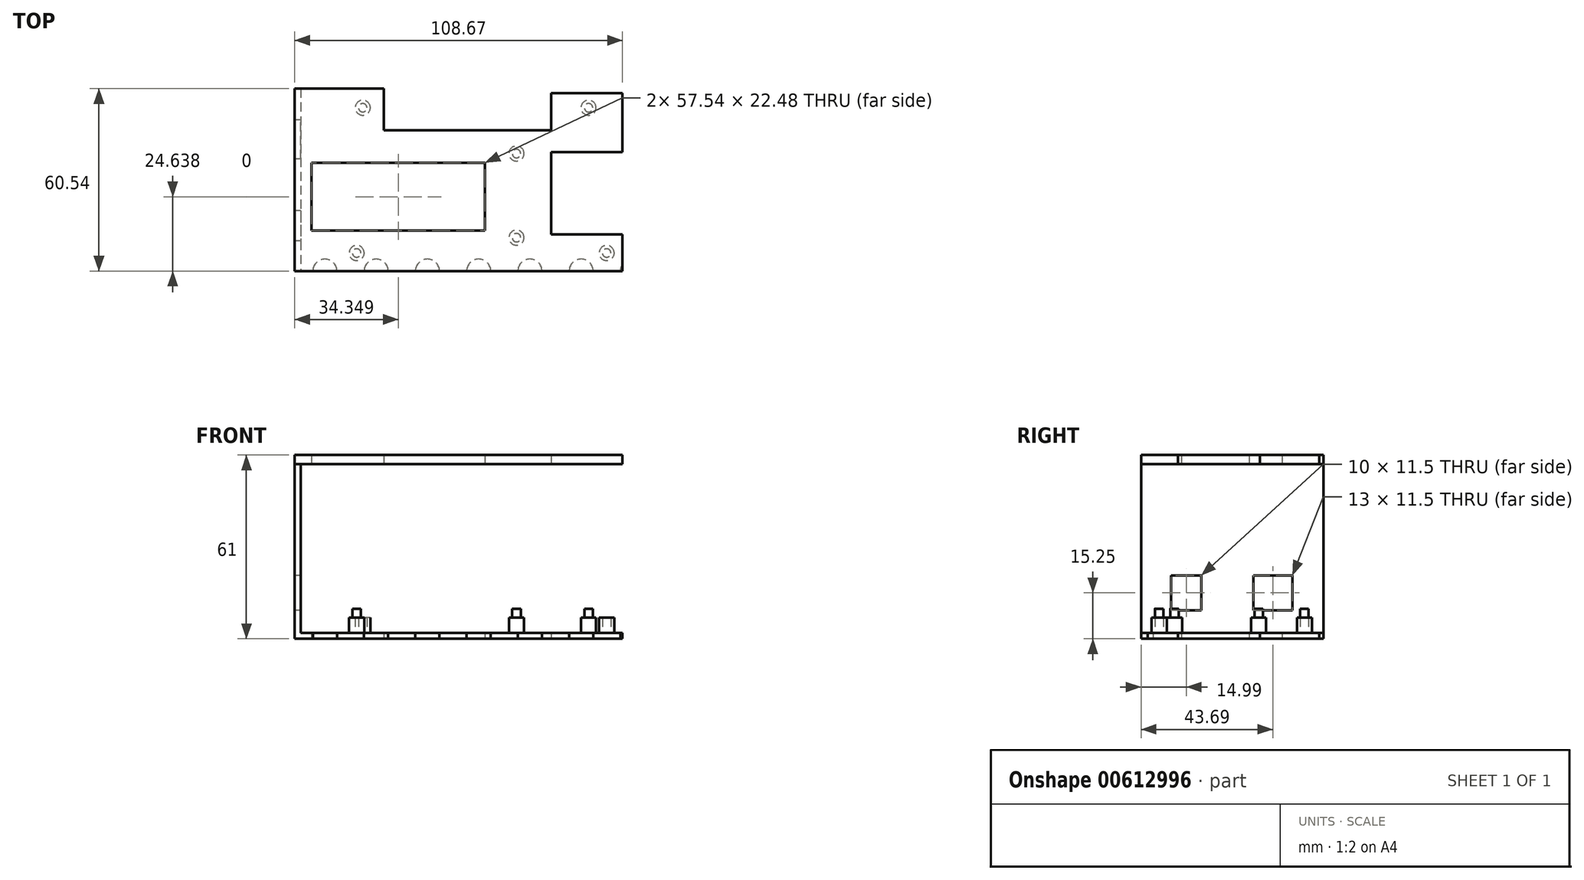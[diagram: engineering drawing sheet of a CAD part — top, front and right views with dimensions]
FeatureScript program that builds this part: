
annotation { "Feature Type Name" : "Feature", "Feature Type Description" : "" }
export const myFeature = defineFeature(function(context is Context, id is Id, definition is map)
    precondition{}
    {
        {
            var Q0;
            Q0=qCreatedBy(makeId("Top.planeOp"),FACE);
            var sketch = newSketch(context, id + "F0", { "sketchPlane" : qUnion([Q0])});
            skLineSegment(sketch, "E0.bottom", {"start": v(-60, 45) * mm, "end": v(60, 45) * mm});
            skLineSegment(sketch, "E0.top", {"start": v(-60, -45) * mm, "end": v(60, -45) * mm});
            skLineSegment(sketch, "E0.left", {"start": v(-60, 45) * mm, "end": v(-60, -45) * mm});
            skLineSegment(sketch, "E0.right", {"start": v(60, 45) * mm, "end": v(60, -45) * mm});
            skPoint(sketch, "E0.middle", {"position": v(0, 0) * mm});
            skLineSegment(sketch, "E1.0", {"start": v(-62, 47) * mm, "end": v(-62, -47) * mm});
            skLineSegment(sketch, "E1.1", {"start": v(-62, 47) * mm, "end": v(62, 47) * mm});
            skLineSegment(sketch, "E1.2", {"start": v(62, 47) * mm, "end": v(62, -47) * mm});
            skLineSegment(sketch, "E1.3", {"start": v(-62, -47) * mm, "end": v(62, -47) * mm});
            skLineSegment(sketch, "E2", {"start": v(60, 31) * mm, "end": v(60, 29) * mm});
            skSolve(sketch);
        }
        {
            var Q0;
            Q0 = qSketchRegion(id + "F0", true);
            var Q1;
            Q1=makeQuery(id+"F0.imprint","IMPRINT",FACE,{"disambiguationData":[TD([[makeQuery(id+"F0.imprint","IMPRINT",EDGE,{"derivedFrom":sQuery(id+"F0.wireOp",EDGE,"E0.bottom")}),-1.0]])]});
            var Q2;
            {var subQ0=sQuery(id+"F0.wireOp",EDGE,"MuUvbIVO-RKHI-1Iq4-MDRf-3431R1IhVsWr");Q2=makeQuery(id+"F0.imprint","IMPRINT",FACE,{"disambiguationData":[TD([[makeQuery(id+"F0.imprint","IMPRINT",EDGE,{"derivedFrom":subQ0}),1.0]])]});}
            var Q3;
            {var subQ0=sQuery(id+"F0.wireOp",EDGE,"E0.top");Q3=makeQuery(id+"F0.imprint","IMPRINT",FACE,{"disambiguationData":[TD([[makeQuery(id+"F0.imprint","IMPRINT",EDGE,{"derivedFrom":subQ0}),1.0]])]});}
            extrude(context, id + "F1", {"entities" : qUnion([Q0, Q1, Q2, Q3]), "depth" : 2 * mm, "offsetDistance" : 25 * mm});
        }
        {
            var Q0;
            Q0=makeQuery(id+"F0.imprint","IMPRINT",FACE,{"disambiguationData":[TD([[makeQuery(id+"F0.imprint","IMPRINT",EDGE,{"derivedFrom":sQuery(id+"F0.wireOp",EDGE,"E0.bottom")}),1.0]])]});
            var Q1;
            {var subQ0=sQuery(id+"F0.wireOp",EDGE,"MuUvbIVO-RKHI-1Iq4-MDRf-3431R1IhVsWr");Q1=makeQuery(id+"F0.imprint","IMPRINT",FACE,{"disambiguationData":[TD([[makeQuery(id+"F0.imprint","IMPRINT",EDGE,{"derivedFrom":subQ0}),1.0]])]});}
            extrude(context, id + "F2", {"entities" : qUnion([Q0, Q1]), "operationType" : NewBodyOperationType.ADD, "depth" : 58 * mm, "offsetDistance" : 25 * mm});
        }
        {
            var Q0;
            Q0=makeQuery(id+"F1.opExtrude","CAP_FACE",FACE,{"disambiguationData":[OSD([sQuery(id+"F0.wireOp",EDGE,"E1.0"),sQuery(id+"F0.wireOp",EDGE,"E1.1"),sQuery(id+"F0.wireOp",EDGE,"E1.2"),sQuery(id+"F0.wireOp",EDGE,"E1.3")])],"isStart":false});
            var sketch = newSketch(context, id + "F3", { "sketchPlane" : qUnion([Q0])});
            skCircle(sketch, "E3", {"center": v(35.45, 23.2) * mm, "radius": 2.5 * mm});
            skCircle(sketch, "E4", {"center": v(11.55, -19.9) * mm, "radius": 2.5 * mm});
            skCircle(sketch, "E5", {"center": v(41.45, -25) * mm, "radius": 2.5 * mm});
            skCircle(sketch, "E6", {"center": v(11.55, 8) * mm, "radius": 2.5 * mm});
            skCircle(sketch, "E7", {"center": v(-39.45, 23.2) * mm, "radius": 2.5 * mm});
            skCircle(sketch, "E8", {"center": v(-41.45, -25) * mm, "radius": 2.5 * mm});
            skSolve(sketch);
        }
        {
            var Q0;
            Q0 = qSketchRegion(id + "F3", true);
            extrude(context, id + "F4", {"entities" : qUnion([Q0]), "operationType" : NewBodyOperationType.ADD, "depth" : 5 * mm, "offsetDistance" : 25 * mm});
        }
        {
            var Q0;
            Q0=makeQuery(id+"F4.opExtrude","CAP_FACE",FACE,{"disambiguationData":[OSD([sQuery(id+"F3.wireOp",EDGE,"E7")])],"isStart":false});
            var sketch = newSketch(context, id + "F5", { "sketchPlane" : qUnion([Q0])});
            skPoint(sketch, "E9", {"position": v(-39.45, 23.2) * mm});
            skPoint(sketch, "E10", {"position": v(-41.45, -25) * mm});
            skPoint(sketch, "E11", {"position": v(11.55, 8) * mm});
            skPoint(sketch, "E12", {"position": v(11.55, -19.9) * mm});
            skPoint(sketch, "E13", {"position": v(41.45, -25) * mm});
            skPoint(sketch, "E14", {"position": v(35.45, 23.2) * mm});
            skCircle(sketch, "E15", {"center": v(-39.45, 23.2) * mm, "radius": 1.4 * mm});
            skCircle(sketch, "E16", {"center": v(-41.45, -25) * mm, "radius": 1.4 * mm});
            skCircle(sketch, "E17", {"center": v(11.55, 8) * mm, "radius": 1.4 * mm});
            skCircle(sketch, "E18", {"center": v(11.55, -19.9) * mm, "radius": 1.4 * mm});
            skCircle(sketch, "E19", {"center": v(41.45, -25) * mm, "radius": 1.4 * mm});
            skCircle(sketch, "E20", {"center": v(35.45, 23.2) * mm, "radius": 1.4 * mm});
            skSolve(sketch);
        }
        {
            var Q0;
            Q0=makeQuery(id+"F5.imprint","IMPRINT",FACE,{"disambiguationData":[TD([[makeQuery(id+"F5.imprint","IMPRINT",EDGE,{"derivedFrom":sQuery(id+"F5.wireOp",EDGE,"E20")}),1.0]])]});
            var Q1;
            Q1=makeQuery(id+"F5.imprint","IMPRINT",FACE,{"disambiguationData":[TD([[makeQuery(id+"F5.imprint","IMPRINT",EDGE,{"derivedFrom":sQuery(id+"F5.wireOp",EDGE,"E17")}),1.0]])]});
            var Q2;
            Q2=makeQuery(id+"F5.imprint","IMPRINT",FACE,{"disambiguationData":[TD([[makeQuery(id+"F5.imprint","IMPRINT",EDGE,{"derivedFrom":sQuery(id+"F5.wireOp",EDGE,"E18")}),1.0]])]});
            var Q3;
            Q3=makeQuery(id+"F5.imprint","IMPRINT",FACE,{"disambiguationData":[TD([[makeQuery(id+"F5.imprint","IMPRINT",EDGE,{"derivedFrom":sQuery(id+"F5.wireOp",EDGE,"E16")}),1.0]])]});
            extrude(context, id + "F6", {"entities" : qUnion([Q0, Q1, Q2, Q3]), "operationType" : NewBodyOperationType.ADD, "depth" : 3 * mm, "offsetDistance" : 25 * mm});
        }
        {
            var Q0;
            Q0=sQuery(id+"F3.wireOp",VERTEX,"E7.center");
            var Q1;
            Q1=sQuery(id+"F3.wireOp",VERTEX,"E5.center");
            var Q2;
            Q2=makeQuery(id+"F1.opExtrude","SWEPT_BODY",BODY,{"disambiguationData":[OSD([sQuery(id+"F0.wireOp",EDGE,"E1.0"),sQuery(id+"F0.wireOp",EDGE,"E1.1"),sQuery(id+"F0.wireOp",EDGE,"E1.2"),sQuery(id+"F0.wireOp",EDGE,"E1.3")])]});
            hole(context, id + "F7", {"style" : HoleStyle.SIMPLE, "endStyle" : HoleEndStyle.BLIND, "oppositeDirection" : true, "holeDiameter" : 2.8 * mm, "majorDiameter" : 5 * mm, "holeDepth" : 5 * mm, "isTappedThrough" : true, "tappedDepth" : 12 * mm, "tapClearance" : 3, "startFromSketch" : true, "locations" : qUnion([Q0, Q1]), "scope" : qUnion([Q2])});
        }
        {
            var Q0;
            Q0=makeQuery(id+"F1.opExtrude","CAP_FACE",FACE,{"disambiguationData":[OSD([sQuery(id+"F0.wireOp",EDGE,"E1.0"),sQuery(id+"F0.wireOp",EDGE,"E1.1"),sQuery(id+"F0.wireOp",EDGE,"E1.2"),sQuery(id+"F0.wireOp",EDGE,"E1.3")])],"isStart":true});
            var sketch = newSketch(context, id + "F8", { "sketchPlane" : qUnion([Q0])});
            skLineSegment(sketch, "E21", {"start": v(-52, 107.06) * mm, "end": v(-52, 15.89) * mm, "construction": true});
            skLineSegment(sketch, "E22", {"start": v(-52, 47) * mm, "end": v(-56, 47) * mm});
            skLineSegment(sketch, "E23", {"start": v(-56, 47) * mm, "end": v(-56, 31) * mm});
            skArc(sketch, "E24", {"start": v(-56, 31) * mm, "mid": v(-54.83, 28.17) * mm, "end": v(-52, 27) * mm});
            skLineSegment(sketch, "E25", {"start": v(-52, 47) * mm, "end": v(-52, 27) * mm});
            skLineSegment(sketch, "E26.MirrorCS", {"start": v(-48, 47) * mm, "end": v(-48, 31) * mm});
            skLineSegment(sketch, "E27.MirrorCS", {"start": v(-52, 47) * mm, "end": v(-48, 47) * mm});
            skArc(sketch, "E28.MirrorCS", {"start": v(-48, 31) * mm, "mid": v(-49.17, 28.17) * mm, "end": v(-52, 27) * mm});
            skLineSegment(sketch, "E29.1.0.0", {"start": v(-35, 47) * mm, "end": v(-39, 47) * mm});
            skLineSegment(sketch, "E29.1.0.1", {"start": v(-39, 47) * mm, "end": v(-39, 31) * mm});
            skLineSegment(sketch, "E29.1.0.2", {"start": v(-31, 47) * mm, "end": v(-31, 31) * mm});
            skArc(sketch, "E29.1.0.3", {"start": v(-31, 31) * mm, "mid": v(-32.17, 28.17) * mm, "end": v(-35, 27) * mm});
            skArc(sketch, "E29.1.0.4", {"start": v(-39, 31) * mm, "mid": v(-37.83, 28.17) * mm, "end": v(-35, 27) * mm});
            skLineSegment(sketch, "E29.2.0.0", {"start": v(-18, 47) * mm, "end": v(-22, 47) * mm});
            skLineSegment(sketch, "E29.2.0.1", {"start": v(-22, 47) * mm, "end": v(-22, 31) * mm});
            skLineSegment(sketch, "E29.2.0.2", {"start": v(-14, 47) * mm, "end": v(-14, 31) * mm});
            skArc(sketch, "E29.2.0.3", {"start": v(-14, 31) * mm, "mid": v(-15.17, 28.17) * mm, "end": v(-18, 27) * mm});
            skArc(sketch, "E29.2.0.4", {"start": v(-22, 31) * mm, "mid": v(-20.83, 28.17) * mm, "end": v(-18, 27) * mm});
            skLineSegment(sketch, "E29.3.0.0", {"start": v(-1, 47) * mm, "end": v(-5, 47) * mm});
            skLineSegment(sketch, "E29.3.0.1", {"start": v(-5, 47) * mm, "end": v(-5, 31) * mm});
            skLineSegment(sketch, "E29.3.0.2", {"start": v(3, 47) * mm, "end": v(3, 31) * mm});
            skArc(sketch, "E29.3.0.3", {"start": v(3, 31) * mm, "mid": v(1.83, 28.17) * mm, "end": v(-1, 27) * mm});
            skArc(sketch, "E29.3.0.4", {"start": v(-5, 31) * mm, "mid": v(-3.83, 28.17) * mm, "end": v(-1, 27) * mm});
            skLineSegment(sketch, "E29.4.0.0", {"start": v(16, 47) * mm, "end": v(12, 47) * mm});
            skLineSegment(sketch, "E29.4.0.1", {"start": v(12, 47) * mm, "end": v(12, 31) * mm});
            skLineSegment(sketch, "E29.4.0.2", {"start": v(20, 47) * mm, "end": v(20, 31) * mm});
            skArc(sketch, "E29.4.0.3", {"start": v(20, 31) * mm, "mid": v(18.83, 28.17) * mm, "end": v(16, 27) * mm});
            skArc(sketch, "E29.4.0.4", {"start": v(12, 31) * mm, "mid": v(13.17, 28.17) * mm, "end": v(16, 27) * mm});
            skLineSegment(sketch, "E29.direction1", {"start": v(-56, 47) * mm, "end": v(-39, 47) * mm, "construction": true});
            skLineSegment(sketch, "E30.0.5.0", {"start": v(33, 47) * mm, "end": v(29, 47) * mm});
            skLineSegment(sketch, "E30.3.5.0", {"start": v(29, 47) * mm, "end": v(29, 31) * mm});
            skLineSegment(sketch, "E30.6.5.0", {"start": v(37, 47) * mm, "end": v(37, 31) * mm});
            skArc(sketch, "E30.9.5.0", {"start": v(37, 31) * mm, "mid": v(35.83, 28.17) * mm, "end": v(33, 27) * mm});
            skArc(sketch, "E30.13.5.0", {"start": v(29, 31) * mm, "mid": v(30.17, 28.17) * mm, "end": v(33, 27) * mm});
            skLineSegment(sketch, "E30.0.6.0", {"start": v(50, 47) * mm, "end": v(46, 47) * mm});
            skLineSegment(sketch, "E30.3.6.0", {"start": v(46, 47) * mm, "end": v(46, 31) * mm});
            skLineSegment(sketch, "E30.6.6.0", {"start": v(54, 47) * mm, "end": v(54, 31) * mm});
            skArc(sketch, "E30.9.6.0", {"start": v(54, 31) * mm, "mid": v(52.83, 28.17) * mm, "end": v(50, 27) * mm});
            skArc(sketch, "E30.13.6.0", {"start": v(46, 31) * mm, "mid": v(47.17, 28.17) * mm, "end": v(50, 27) * mm});
            skSolve(sketch);
        }
        {
            var Q0;
            Q0=makeQuery(id+"F8.imprint","IMPRINT",FACE,{"disambiguationData":[TD([[makeQuery(id+"F8.imprint","IMPRINT",EDGE,{"derivedFrom":sQuery(id+"F8.wireOp",EDGE,"E22")}),-1.0]])]});
            var Q1;
            Q1=makeQuery(id+"F8.imprint","IMPRINT",FACE,{"disambiguationData":[TD([[makeQuery(id+"F8.imprint","IMPRINT",EDGE,{"derivedFrom":sQuery(id+"F8.wireOp",EDGE,"E25")}),1.0]])]});
            var Q2;
            {var subQ0=sQuery(id+"F8.wireOp",EDGE,"E29.1.0.0");Q2=makeQuery(id+"F8.imprint","IMPRINT",FACE,{"disambiguationData":[TD([[makeQuery(id+"F8.imprint","IMPRINT",EDGE,{"derivedFrom":subQ0}),-1.0]])]});}
            var Q3;
            {var subQ1=sQuery(id+"F8.wireOp",EDGE,"E29.2.0.0");Q3=makeQuery(id+"F8.imprint","IMPRINT",FACE,{"disambiguationData":[TD([[makeQuery(id+"F8.imprint","IMPRINT",EDGE,{"derivedFrom":subQ1}),-1.0]])]});}
            var Q4;
            {var subQ1=sQuery(id+"F8.wireOp",EDGE,"E29.3.0.0");Q4=makeQuery(id+"F8.imprint","IMPRINT",FACE,{"disambiguationData":[TD([[makeQuery(id+"F8.imprint","IMPRINT",EDGE,{"derivedFrom":subQ1}),-1.0]])]});}
            var Q5;
            {var subQ1=sQuery(id+"F8.wireOp",EDGE,"E29.4.0.0");Q5=makeQuery(id+"F8.imprint","IMPRINT",FACE,{"disambiguationData":[TD([[makeQuery(id+"F8.imprint","IMPRINT",EDGE,{"derivedFrom":subQ1}),-1.0]])]});}
            var Q6;
            {var subQ1=sQuery(id+"F8.wireOp",EDGE,"E30.0.5.0");Q6=makeQuery(id+"F8.imprint","IMPRINT",FACE,{"disambiguationData":[TD([[makeQuery(id+"F8.imprint","IMPRINT",EDGE,{"derivedFrom":subQ1}),-1.0]])]});}
            var Q7;
            {var subQ1=sQuery(id+"F8.wireOp",EDGE,"E30.0.6.0");Q7=makeQuery(id+"F8.imprint","IMPRINT",FACE,{"disambiguationData":[TD([[makeQuery(id+"F8.imprint","IMPRINT",EDGE,{"derivedFrom":subQ1}),-1.0]])]});}
            extrude(context, id + "F9", {"entities" : qUnion([Q0, Q1, Q2, Q3, Q4, Q5, Q6, Q7]), "operationType" : NewBodyOperationType.REMOVE, "oppositeDirection" : true, "depth" : 8 * mm, "offsetDistance" : 25 * mm});
        }
        {
            var Q0;
            Q0=makeQuery(id+"F2.opExtrude","SWEPT_FACE",FACE,{"disambiguationData":[OSD([sQuery(id+"F0.wireOp",EDGE,"E0.bottom")])]});
            var sketch = newSketch(context, id + "F10", { "sketchPlane" : qUnion([Q0])});
            skLineSegment(sketch, "E31", {"start": v(-42.5, 52) * mm, "end": v(-42.5, 2) * mm});
            skLineSegment(sketch, "E32", {"start": v(-42.5, 2) * mm, "end": v(-41.5, 2) * mm});
            skLineSegment(sketch, "E33", {"start": v(-41.5, 2) * mm, "end": v(-41.5, 52) * mm});
            skLineSegment(sketch, "E34", {"start": v(-41.5, 52) * mm, "end": v(-42.5, 52) * mm});
            skLineSegment(sketch, "E35", {"start": v(-40, 64) * mm, "end": v(-40, -2.7) * mm, "construction": true});
            skLineSegment(sketch, "E36.MirrorCS", {"start": v(-38.5, 2) * mm, "end": v(-38.5, 52) * mm});
            skLineSegment(sketch, "E37.MirrorCS", {"start": v(-37.5, 52) * mm, "end": v(-37.5, 2) * mm});
            skLineSegment(sketch, "E38.MirrorCS", {"start": v(-38.5, 52) * mm, "end": v(-37.5, 52) * mm});
            skLineSegment(sketch, "E39.MirrorCS", {"start": v(-37.5, 2) * mm, "end": v(-38.5, 2) * mm});
            skLineSegment(sketch, "E40", {"start": v(-20, 58) * mm, "end": v(-20, 0) * mm, "construction": true});
            skLineSegment(sketch, "E41.MirrorCS", {"start": v(1.5, 52) * mm, "end": v(2.5, 52) * mm});
            skLineSegment(sketch, "E42.MirrorCS", {"start": v(2.5, 2) * mm, "end": v(1.5, 2) * mm});
            skLineSegment(sketch, "E43.MirrorCS", {"start": v(-2.5, 2) * mm, "end": v(-1.5, 2) * mm});
            skLineSegment(sketch, "E44.MirrorCS", {"start": v(-1.5, 52) * mm, "end": v(-2.5, 52) * mm});
            skLineSegment(sketch, "E45.MirrorCS", {"start": v(-1.5, 2) * mm, "end": v(-1.5, 52) * mm});
            skLineSegment(sketch, "E46.MirrorCS", {"start": v(1.5, 2) * mm, "end": v(1.5, 52) * mm});
            skLineSegment(sketch, "E47.MirrorCS", {"start": v(0, 64) * mm, "end": v(0, -2.7) * mm, "construction": true});
            skLineSegment(sketch, "E48.MirrorCS", {"start": v(2.5, 52) * mm, "end": v(2.5, 2) * mm});
            skLineSegment(sketch, "E49.MirrorCS", {"start": v(-2.5, 52) * mm, "end": v(-2.5, 2) * mm});
            skLineSegment(sketch, "E50", {"start": v(20, 58) * mm, "end": v(20, -6.5) * mm, "construction": true});
            skLineSegment(sketch, "E51.MirrorCS", {"start": v(38.5, 52) * mm, "end": v(37.5, 52) * mm});
            skLineSegment(sketch, "E52.MirrorCS", {"start": v(37.5, 2) * mm, "end": v(38.5, 2) * mm});
            skLineSegment(sketch, "E53.MirrorCS", {"start": v(41.5, 52) * mm, "end": v(42.5, 52) * mm});
            skLineSegment(sketch, "E54.MirrorCS", {"start": v(42.5, 2) * mm, "end": v(41.5, 2) * mm});
            skLineSegment(sketch, "E55.MirrorCS", {"start": v(42.5, 52) * mm, "end": v(42.5, 2) * mm});
            skLineSegment(sketch, "E56.MirrorCS", {"start": v(38.5, 2) * mm, "end": v(38.5, 52) * mm});
            skLineSegment(sketch, "E57.MirrorCS", {"start": v(37.5, 52) * mm, "end": v(37.5, 2) * mm});
            skLineSegment(sketch, "E58.MirrorCS", {"start": v(41.5, 2) * mm, "end": v(41.5, 52) * mm});
            skLineSegment(sketch, "E59.MirrorCS", {"start": v(40, 64) * mm, "end": v(40, -2.7) * mm, "construction": true});
            skSolve(sketch);
        }
        {
            var Q0;
            Q0 = qSketchRegion(id + "F10", true);
            extrude(context, id + "F11", {"entities" : qUnion([Q0]), "operationType" : NewBodyOperationType.ADD, "depth" : 3 * mm, "offsetDistance" : 25 * mm});
        }
        {
            var Q0;
            Q0=makeQuery(id+"F11.opExtrude","CAP_FACE",FACE,{"disambiguationData":[OSD([sQuery(id+"F10.wireOp",EDGE,"E31"),sQuery(id+"F10.wireOp",EDGE,"E32"),sQuery(id+"F10.wireOp",EDGE,"E33"),sQuery(id+"F10.wireOp",EDGE,"E34")])],"isStart":false});
            var sketch = newSketch(context, id + "F12", { "sketchPlane" : qUnion([Q0])});
            skLineSegment(sketch, "E60", {"start": v(-20, 58) * mm, "end": v(-20, 2) * mm});
            skLineSegment(sketch, "E61.MirrorCS", {"start": v(-2.5, 52) * mm, "end": v(2.5, 52) * mm});
            skLineSegment(sketch, "E62.MirrorCS", {"start": v(2.5, 49) * mm, "end": v(-2.5, 49) * mm});
            skLineSegment(sketch, "E63.MirrorCS", {"start": v(2.5, 49) * mm, "end": v(2.5, 52) * mm});
            skLineSegment(sketch, "E64.MirrorCS", {"start": v(-2.5, 49) * mm, "end": v(-2.5, 52) * mm});
            skLineSegment(sketch, "E65", {"start": v(20, 58) * mm, "end": v(20, 2) * mm});
            skLineSegment(sketch, "E66.0.1.0", {"start": v(-2.5, 41) * mm, "end": v(-2.5, 44) * mm});
            skLineSegment(sketch, "E66.0.1.1", {"start": v(2.5, 41) * mm, "end": v(2.5, 44) * mm});
            skLineSegment(sketch, "E66.0.1.2", {"start": v(2.5, 41) * mm, "end": v(-2.5, 41) * mm});
            skLineSegment(sketch, "E66.0.1.3", {"start": v(-2.5, 44) * mm, "end": v(2.5, 44) * mm});
            skLineSegment(sketch, "E66.0.2.0", {"start": v(-2.5, 34) * mm, "end": v(-2.5, 37) * mm});
            skLineSegment(sketch, "E66.0.2.1", {"start": v(2.5, 34) * mm, "end": v(2.5, 37) * mm});
            skLineSegment(sketch, "E66.0.2.2", {"start": v(2.5, 34) * mm, "end": v(-2.5, 34) * mm});
            skLineSegment(sketch, "E66.0.2.3", {"start": v(-2.5, 37) * mm, "end": v(2.5, 37) * mm});
            skLineSegment(sketch, "E66.0.3.0", {"start": v(-2.5, 26) * mm, "end": v(-2.5, 29) * mm});
            skLineSegment(sketch, "E66.0.3.1", {"start": v(2.5, 26) * mm, "end": v(2.5, 29) * mm});
            skLineSegment(sketch, "E66.0.3.2", {"start": v(2.5, 26) * mm, "end": v(-2.5, 26) * mm});
            skLineSegment(sketch, "E66.0.3.3", {"start": v(-2.5, 29) * mm, "end": v(2.5, 29) * mm});
            skLineSegment(sketch, "E66.0.4.0", {"start": v(-2.5, 18) * mm, "end": v(-2.5, 21) * mm});
            skLineSegment(sketch, "E66.0.4.1", {"start": v(2.5, 18) * mm, "end": v(2.5, 21) * mm});
            skLineSegment(sketch, "E66.0.4.2", {"start": v(2.5, 18) * mm, "end": v(-2.5, 18) * mm});
            skLineSegment(sketch, "E66.0.4.3", {"start": v(-2.5, 21) * mm, "end": v(2.5, 21) * mm});
            skLineSegment(sketch, "E66.0.5.0", {"start": v(-2.5, 10) * mm, "end": v(-2.5, 13) * mm});
            skLineSegment(sketch, "E66.0.5.1", {"start": v(2.5, 10) * mm, "end": v(2.5, 13) * mm});
            skLineSegment(sketch, "E66.0.5.2", {"start": v(2.5, 10) * mm, "end": v(-2.5, 10) * mm});
            skLineSegment(sketch, "E66.0.5.3", {"start": v(-2.5, 13) * mm, "end": v(2.5, 13) * mm});
            skLineSegment(sketch, "E66.direction2", {"start": v(-2.5, 49) * mm, "end": v(-2.5, 41) * mm, "construction": true});
            skLineSegment(sketch, "E67.MirrorCS", {"start": v(37.5, 18) * mm, "end": v(37.5, 21) * mm});
            skLineSegment(sketch, "E68.MirrorCS", {"start": v(37.5, 41) * mm, "end": v(37.5, 44) * mm});
            skLineSegment(sketch, "E69.MirrorCS", {"start": v(37.5, 49) * mm, "end": v(37.5, 52) * mm});
            skLineSegment(sketch, "E70.MirrorCS", {"start": v(37.5, 34) * mm, "end": v(37.5, 37) * mm});
            skLineSegment(sketch, "E71.MirrorCS", {"start": v(37.5, 26) * mm, "end": v(37.5, 29) * mm});
            skLineSegment(sketch, "E72.MirrorCS", {"start": v(42.5, 34) * mm, "end": v(42.5, 37) * mm});
            skLineSegment(sketch, "E73.MirrorCS", {"start": v(42.5, 41) * mm, "end": v(42.5, 44) * mm});
            skLineSegment(sketch, "E74.MirrorCS", {"start": v(42.5, 26) * mm, "end": v(42.5, 29) * mm});
            skLineSegment(sketch, "E75.MirrorCS", {"start": v(42.5, 10) * mm, "end": v(42.5, 13) * mm});
            skLineSegment(sketch, "E76.MirrorCS", {"start": v(42.5, 18) * mm, "end": v(42.5, 21) * mm});
            skLineSegment(sketch, "E77.MirrorCS", {"start": v(42.5, 49) * mm, "end": v(42.5, 52) * mm});
            skLineSegment(sketch, "E78.MirrorCS", {"start": v(37.5, 10) * mm, "end": v(37.5, 13) * mm});
            skLineSegment(sketch, "E79.MirrorCS", {"start": v(42.5, 21) * mm, "end": v(37.5, 21) * mm});
            skLineSegment(sketch, "E80.MirrorCS", {"start": v(42.5, 13) * mm, "end": v(37.5, 13) * mm});
            skLineSegment(sketch, "E81.MirrorCS", {"start": v(37.5, 10) * mm, "end": v(42.5, 10) * mm});
            skLineSegment(sketch, "E82.MirrorCS", {"start": v(42.5, 52) * mm, "end": v(37.5, 52) * mm});
            skLineSegment(sketch, "E83.MirrorCS", {"start": v(37.5, 18) * mm, "end": v(42.5, 18) * mm});
            skLineSegment(sketch, "E84.MirrorCS", {"start": v(37.5, 49) * mm, "end": v(42.5, 49) * mm});
            skLineSegment(sketch, "E85.MirrorCS", {"start": v(37.5, 26) * mm, "end": v(42.5, 26) * mm});
            skLineSegment(sketch, "E86.MirrorCS", {"start": v(37.5, 34) * mm, "end": v(42.5, 34) * mm});
            skLineSegment(sketch, "E87.MirrorCS", {"start": v(42.5, 29) * mm, "end": v(37.5, 29) * mm});
            skLineSegment(sketch, "E88.MirrorCS", {"start": v(37.5, 41) * mm, "end": v(42.5, 41) * mm});
            skLineSegment(sketch, "E89.MirrorCS", {"start": v(42.5, 49) * mm, "end": v(42.5, 41) * mm, "construction": true});
            skLineSegment(sketch, "E90.MirrorCS", {"start": v(42.5, 37) * mm, "end": v(37.5, 37) * mm});
            skLineSegment(sketch, "E91.MirrorCS", {"start": v(42.5, 44) * mm, "end": v(37.5, 44) * mm});
            skLineSegment(sketch, "E92.MirrorCS", {"start": v(-37.5, 18) * mm, "end": v(-37.5, 21) * mm});
            skLineSegment(sketch, "E93.MirrorCS", {"start": v(-42.5, 18) * mm, "end": v(-42.5, 21) * mm});
            skLineSegment(sketch, "E94.MirrorCS", {"start": v(-37.5, 49) * mm, "end": v(-37.5, 52) * mm});
            skLineSegment(sketch, "E95.MirrorCS", {"start": v(-42.5, 26) * mm, "end": v(-42.5, 29) * mm});
            skLineSegment(sketch, "E96.MirrorCS", {"start": v(-42.5, 34) * mm, "end": v(-42.5, 37) * mm});
            skLineSegment(sketch, "E97.MirrorCS", {"start": v(-37.5, 26) * mm, "end": v(-37.5, 29) * mm});
            skLineSegment(sketch, "E98.MirrorCS", {"start": v(-42.5, 10) * mm, "end": v(-42.5, 13) * mm});
            skLineSegment(sketch, "E99.MirrorCS", {"start": v(-42.5, 41) * mm, "end": v(-42.5, 44) * mm});
            skLineSegment(sketch, "E100.MirrorCS", {"start": v(-37.5, 34) * mm, "end": v(-37.5, 37) * mm});
            skLineSegment(sketch, "E101.MirrorCS", {"start": v(-42.5, 49) * mm, "end": v(-42.5, 52) * mm});
            skLineSegment(sketch, "E102.MirrorCS", {"start": v(-37.5, 41) * mm, "end": v(-37.5, 44) * mm});
            skLineSegment(sketch, "E103.MirrorCS", {"start": v(-37.5, 10) * mm, "end": v(-37.5, 13) * mm});
            skLineSegment(sketch, "E104.MirrorCS", {"start": v(-42.5, 34) * mm, "end": v(-37.5, 34) * mm});
            skLineSegment(sketch, "E105.MirrorCS", {"start": v(-42.5, 10) * mm, "end": v(-37.5, 10) * mm});
            skLineSegment(sketch, "E106.MirrorCS", {"start": v(-37.5, 37) * mm, "end": v(-42.5, 37) * mm});
            skLineSegment(sketch, "E107.MirrorCS", {"start": v(-37.5, 21) * mm, "end": v(-42.5, 21) * mm});
            skLineSegment(sketch, "E108.MirrorCS", {"start": v(-42.5, 18) * mm, "end": v(-37.5, 18) * mm});
            skLineSegment(sketch, "E109.MirrorCS", {"start": v(-42.5, 26) * mm, "end": v(-37.5, 26) * mm});
            skLineSegment(sketch, "E110.MirrorCS", {"start": v(-37.5, 44) * mm, "end": v(-42.5, 44) * mm});
            skLineSegment(sketch, "E111.MirrorCS", {"start": v(-42.5, 49) * mm, "end": v(-37.5, 49) * mm});
            skLineSegment(sketch, "E112.MirrorCS", {"start": v(-37.5, 13) * mm, "end": v(-42.5, 13) * mm});
            skLineSegment(sketch, "E113.MirrorCS", {"start": v(-37.5, 29) * mm, "end": v(-42.5, 29) * mm});
            skLineSegment(sketch, "E114.MirrorCS", {"start": v(-37.5, 52) * mm, "end": v(-42.5, 52) * mm});
            skLineSegment(sketch, "E115.MirrorCS", {"start": v(-42.5, 41) * mm, "end": v(-37.5, 41) * mm});
            skLineSegment(sketch, "E116.MirrorCS", {"start": v(-37.5, 49) * mm, "end": v(-37.5, 41) * mm, "construction": true});
            skSolve(sketch);
        }
        {
            var Q0;
            Q0 = qSketchRegion(id + "F12", true);
            extrude(context, id + "F13", {"entities" : qUnion([Q0]), "operationType" : NewBodyOperationType.ADD, "oppositeDirection" : true, "depth" : 1 * mm, "offsetDistance" : 25 * mm});
        }
        {
            var Q0;
            Q0=makeQuery(id+"F2.opExtrude","CAP_FACE",FACE,{"disambiguationData":[OSD([sQuery(id+"F0.wireOp",EDGE,"E0.bottom"),sQuery(id+"F0.wireOp",EDGE,"E0.top"),sQuery(id+"F0.wireOp",EDGE,"E0.left"),sQuery(id+"F0.wireOp",EDGE,"E0.right"),sQuery(id+"F0.wireOp",EDGE,"E1.0"),sQuery(id+"F0.wireOp",EDGE,"E1.1"),sQuery(id+"F0.wireOp",EDGE,"E1.2"),sQuery(id+"F0.wireOp",EDGE,"E1.3"),sQuery(id+"F0.wireOp",EDGE,"E2")])],"isStart":false});
            var sketch = newSketch(context, id + "F14", { "sketchPlane" : qUnion([Q0])});
            skLineSegment(sketch, "E117.bottom", {"start": v(-62, -47) * mm, "end": v(62, -47) * mm});
            skLineSegment(sketch, "E117.top", {"start": v(-62, 47) * mm, "end": v(62, 47) * mm});
            skLineSegment(sketch, "E117.left", {"start": v(-62, -47) * mm, "end": v(-62, 47) * mm});
            skLineSegment(sketch, "E117.right", {"start": v(62, -47) * mm, "end": v(62, 47) * mm});
            skSolve(sketch);
        }
        {
            var Q0;
            Q0 = qSketchRegion(id + "F14", true);
            extrude(context, id + "F15", {"entities" : qUnion([Q0]), "depth" : 3 * mm, "offsetDistance" : 25 * mm});
        }
        {
            var Q0;
            Q0=qCreatedBy(makeId("Top.planeOp"),FACE);
            cPlane(context, id + "F16", {"entities" : qUnion([Q0]), "cplaneType" : CPlaneType.OFFSET, "offset" : 9.5 * mm, "width" : 150 * mm, "height" : 150 * mm});
        }
        {
            var Q0;
            Q0=qCreatedBy(id+"F16.planeOp",FACE);
            var sketch = newSketch(context, id + "F17", { "sketchPlane" : qUnion([Q0])});
            skLineSegment(sketch, "E118.bottom", {"start": v(-60, 6.2) * mm, "end": v(-62, 6.2) * mm});
            skLineSegment(sketch, "E118.top", {"start": v(-60, 19.2) * mm, "end": v(-62, 19.2) * mm});
            skLineSegment(sketch, "E118.left", {"start": v(-60, 6.2) * mm, "end": v(-60, 19.2) * mm});
            skLineSegment(sketch, "E118.right", {"start": v(-62, 6.2) * mm, "end": v(-62, 19.2) * mm});
            skLineSegment(sketch, "E119.bottom", {"start": v(-60, -11) * mm, "end": v(-62, -11) * mm});
            skLineSegment(sketch, "E119.top", {"start": v(-60, -21) * mm, "end": v(-62, -21) * mm});
            skLineSegment(sketch, "E119.left", {"start": v(-60, -11) * mm, "end": v(-60, -21) * mm});
            skLineSegment(sketch, "E119.right", {"start": v(-62, -11) * mm, "end": v(-62, -21) * mm});
            skSolve(sketch);
        }
        {
            var Q0;
            Q0 = qSketchRegion(id + "F17", true);
            extrude(context, id + "F18", {"entities" : qUnion([Q0]), "operationType" : NewBodyOperationType.REMOVE, "depth" : 11.5 * mm, "offsetDistance" : 25 * mm});
        }
        {
            var Q0;
            Q0=qCreatedBy(makeId("Top.planeOp"),FACE);
            var sketch = newSketch(context, id + "F19", { "sketchPlane" : qUnion([Q0])});
            skLineSegment(sketch, "E120", {"start": v(-68.1, 29.55) * mm, "end": v(-32.42, 29.55) * mm});
            skLineSegment(sketch, "E121", {"start": v(-32.42, 29.55) * mm, "end": v(-32.42, 15.72) * mm});
            skLineSegment(sketch, "E122", {"start": v(-32.42, 15.72) * mm, "end": v(23.07, 15.72) * mm});
            skLineSegment(sketch, "E123", {"start": v(23.07, 15.72) * mm, "end": v(23.07, 28.08) * mm});
            skLineSegment(sketch, "E124", {"start": v(23.07, 28.08) * mm, "end": v(46.67, 28.08) * mm});
            skLineSegment(sketch, "E125", {"start": v(23.07, -18.8) * mm, "end": v(46.67, -18.8) * mm});
            skLineSegment(sketch, "E126", {"start": v(46.67, -18.8) * mm, "end": v(46.67, -31) * mm});
            skLineSegment(sketch, "E127", {"start": v(46.67, -31) * mm, "end": v(-68.1, -31) * mm});
            skLineSegment(sketch, "E128", {"start": v(-68.1, -31) * mm, "end": v(-68.1, 29.55) * mm});
            skLineSegment(sketch, "E129", {"start": v(-56.42, 4.89) * mm, "end": v(1.12, 4.89) * mm});
            skLineSegment(sketch, "E130", {"start": v(1.12, 4.89) * mm, "end": v(1.12, -17.6) * mm});
            skLineSegment(sketch, "E131", {"start": v(1.12, -17.6) * mm, "end": v(-56.42, -17.6) * mm});
            skLineSegment(sketch, "E132", {"start": v(-56.42, -17.6) * mm, "end": v(-56.42, 4.89) * mm});
            skLineSegment(sketch, "E133.bottom", {"start": v(-97.16, 70.48) * mm, "end": v(102.36, 70.48) * mm});
            skLineSegment(sketch, "E133.top", {"start": v(-97.16, -73.06) * mm, "end": v(102.36, -73.06) * mm});
            skLineSegment(sketch, "E133.left", {"start": v(-97.16, 70.48) * mm, "end": v(-97.16, -73.06) * mm});
            skLineSegment(sketch, "E133.right", {"start": v(102.36, 70.48) * mm, "end": v(102.36, -73.06) * mm});
            skLineSegment(sketch, "E134", {"start": v(23.07, -18.8) * mm, "end": v(23.07, 8.46) * mm});
            skLineSegment(sketch, "E135", {"start": v(23.07, 8.46) * mm, "end": v(46.67, 8.46) * mm});
            skLineSegment(sketch, "E136", {"start": v(46.67, 8.46) * mm, "end": v(46.67, 28.08) * mm});
            skSolve(sketch);
        }
        {
            var Q0;
            Q0 = qSketchRegion(id + "F19", true);
            var Q1;
            Q1=makeQuery(id+"F19.imprint","IMPRINT",FACE,{"disambiguationData":[TD([[makeQuery(id+"F19.imprint","IMPRINT",EDGE,{"derivedFrom":sQuery(id+"F19.wireOp",EDGE,"E129")}),-1.0]])]});
            extrude(context, id + "F20", {"entities" : qUnion([Q0, Q1]), "operationType" : NewBodyOperationType.REMOVE, "depth" : 100 * mm, "offsetDistance" : 25 * mm});
        }
    });
